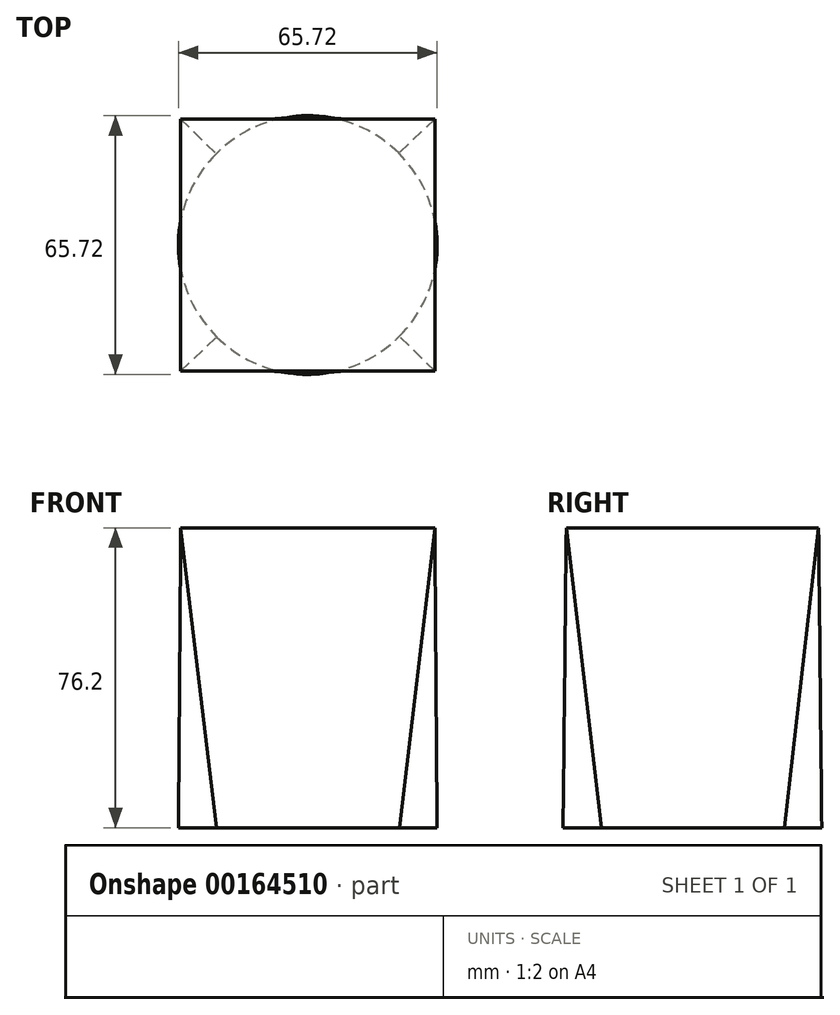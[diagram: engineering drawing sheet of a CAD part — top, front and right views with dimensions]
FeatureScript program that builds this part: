
annotation { "Feature Type Name" : "Feature", "Feature Type Description" : "" }
export const myFeature = defineFeature(function(context is Context, id is Id, definition is map)
    precondition{}
    {
        {
            var Q0;
            Q0=qCreatedBy(makeId("Top.planeOp"),FACE);
            var sketch = newSketch(context, id + "F0", { "sketchPlane" : qUnion([Q0])});
            skCircle(sketch, "E0", {"center": v(0, 0) * mm, "radius": 32.86 * mm});
            skSolve(sketch);
        }
        {
            var Q0;
            Q0=qCreatedBy(makeId("Top.planeOp"),FACE);
            cPlane(context, id + "F1", {"entities" : qUnion([Q0]), "cplaneType" : CPlaneType.OFFSET, "offset" : 76.2 * mm, "width" : 152.4 * mm, "height" : 152.4 * mm});
        }
        {
            var Q0;
            Q0=qCreatedBy(id+"F1.planeOp",FACE);
            var sketch = newSketch(context, id + "F2", { "sketchPlane" : qUnion([Q0])});
            skLineSegment(sketch, "E1.bottom", {"start": v(-32.28, 32.05) * mm, "end": v(32.28, 32.05) * mm});
            skLineSegment(sketch, "E1.top", {"start": v(-32.28, -32.05) * mm, "end": v(32.28, -32.05) * mm});
            skLineSegment(sketch, "E1.left", {"start": v(-32.28, 32.05) * mm, "end": v(-32.28, -32.05) * mm});
            skLineSegment(sketch, "E1.right", {"start": v(32.28, 32.05) * mm, "end": v(32.28, -32.05) * mm});
            skPoint(sketch, "E1.middle", {"position": v(0, 0) * mm});
            skSolve(sketch);
        }
        {
            var Q0;
            Q0=makeQuery(id+"F2.imprint","IMPRINT",FACE,{"disambiguationData":[TD([[makeQuery(id+"F2.imprint","IMPRINT",EDGE,{"derivedFrom":sQuery(id+"F2.wireOp",EDGE,"E1.bottom")}),-1.0]])]});
            var Q1;
            Q1=makeQuery(id+"F0.imprint","IMPRINT",FACE,{"disambiguationData":[TD([[makeQuery(id+"F0.imprint","IMPRINT",EDGE,{"derivedFrom":sQuery(id+"F0.wireOp",EDGE,"E0")}),1.0]])]});
            loft(context, id + "F3", {"sheetProfilesArray" : [{ "sheetProfileEntities" : qUnion([Q0]) }, { "sheetProfileEntities" : qUnion([Q1]) }]});
        }
    });
